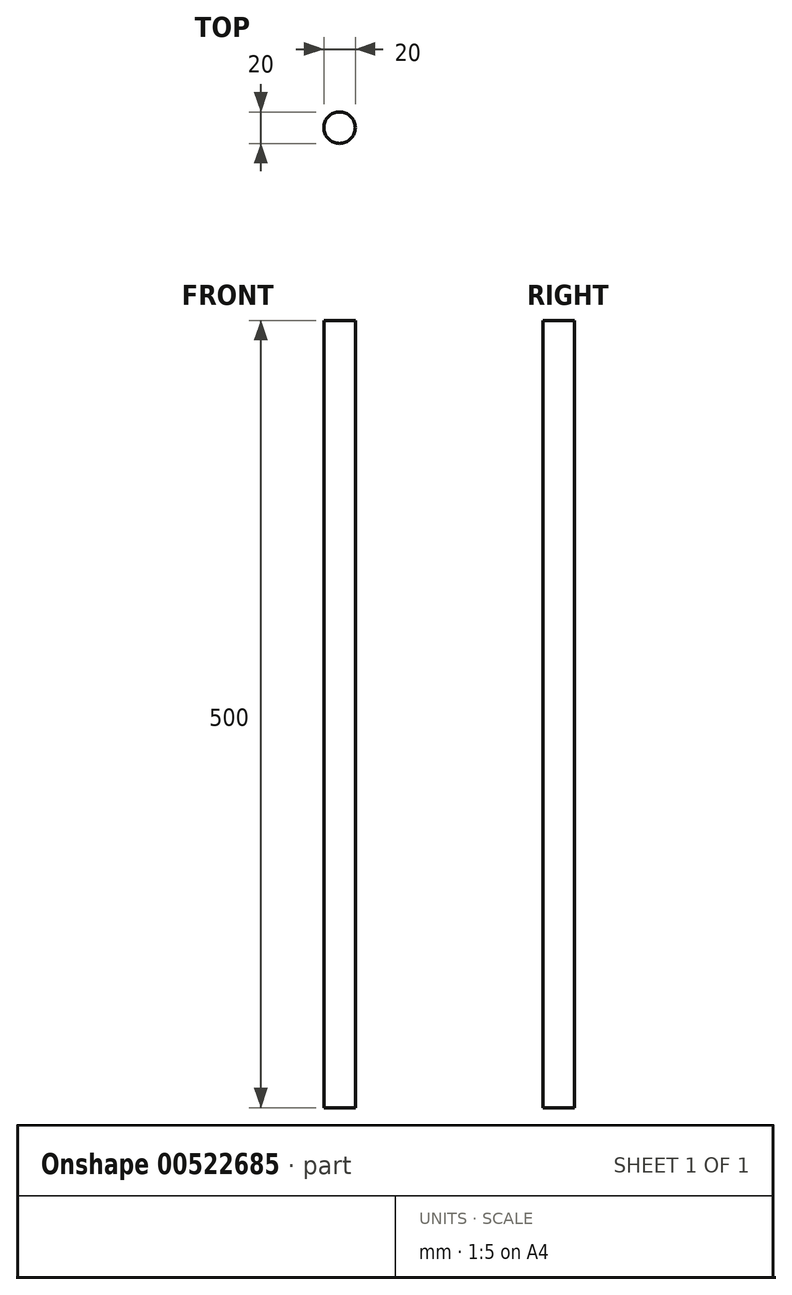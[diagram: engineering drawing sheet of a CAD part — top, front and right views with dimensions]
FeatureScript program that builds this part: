
annotation { "Feature Type Name" : "Feature", "Feature Type Description" : "" }
export const myFeature = defineFeature(function(context is Context, id is Id, definition is map)
    precondition{}
    {
        {
            var Q0;
            Q0=qCreatedBy(makeId("Top.planeOp"),FACE);
            var sketch = newSketch(context, id + "F0", { "sketchPlane" : qUnion([Q0])});
            skCircle(sketch, "E0", {"center": v(0, 0) * mm, "radius": 10 * mm});
            skSolve(sketch);
        }
        {
            var Q0;
            Q0=qSketchRegion(id+"F0",true);
            extrude(context, id + "F1", {"entities" : qUnion([Q0]), "depth" : 500 * mm, "offsetDistance" : 25 * mm});
        }
    });
